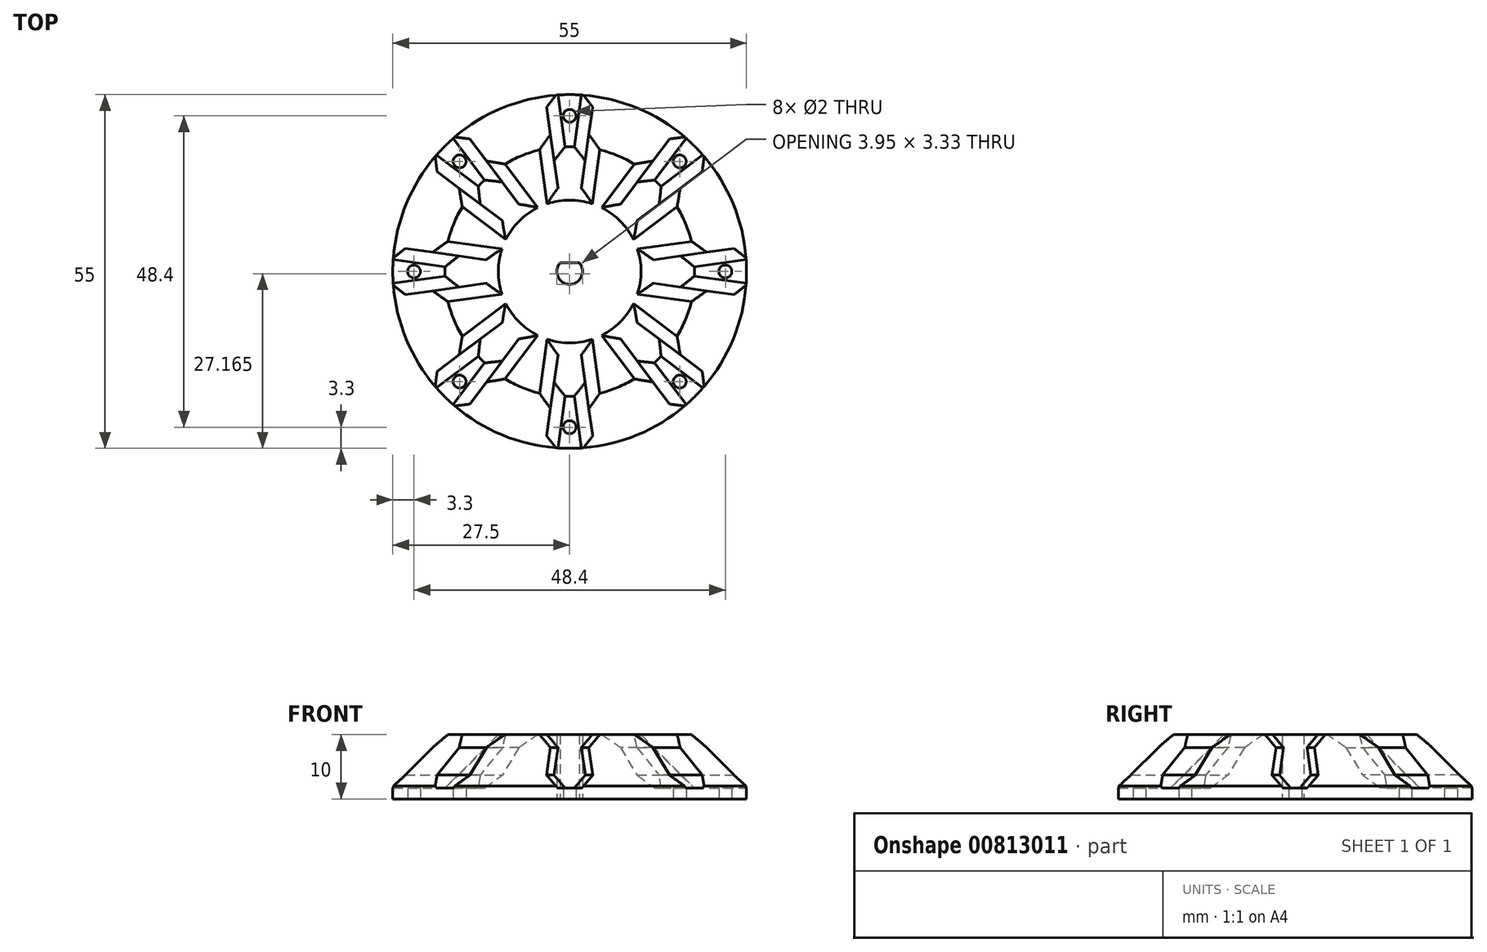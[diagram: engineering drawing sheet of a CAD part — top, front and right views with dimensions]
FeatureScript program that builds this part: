
annotation { "Feature Type Name" : "Feature", "Feature Type Description" : "" }
export const myFeature = defineFeature(function(context is Context, id is Id, definition is map)
    precondition{}
    {
        {
            var Q0;
            Q0=qCreatedBy(makeId("Top.planeOp"),FACE);
            var sketch = newSketch(context, id + "F0", { "sketchPlane" : qUnion([Q0])});
            skCircle(sketch, "E0", {"center": v(0, 0) * mm, "radius": 27.5 * mm});
            skCircle(sketch, "E1.0", {"center": v(0, 0) * mm, "radius": 21.1 * mm});
            skCircle(sketch, "E2", {"center": v(0, 24.2) * mm, "radius": 1 * mm});
            skCircle(sketch, "E3.1.0", {"center": v(-17.11, 17.11) * mm, "radius": 1 * mm});
            skCircle(sketch, "E3.2.0", {"center": v(-24.2, 0) * mm, "radius": 1 * mm});
            skCircle(sketch, "E3.3.0", {"center": v(-17.11, -17.11) * mm, "radius": 1 * mm});
            skCircle(sketch, "E3.4.0", {"center": v(0, -24.2) * mm, "radius": 1 * mm});
            skCircle(sketch, "E3.5.0", {"center": v(17.11, -17.11) * mm, "radius": 1 * mm});
            skCircle(sketch, "E3.6.0", {"center": v(24.2, 0) * mm, "radius": 1 * mm});
            skCircle(sketch, "E3.7.0", {"center": v(17.11, 17.11) * mm, "radius": 1 * mm});
            skLineSegment(sketch, "E4", {"start": v(0, 0) * mm, "end": v(3.83, 27.23) * mm});
            skLineSegment(sketch, "E5", {"start": v(0, 0) * mm, "end": v(16.55, 21.96) * mm});
            skLineSegment(sketch, "E6.1.0", {"start": v(0, 0) * mm, "end": v(-3.83, 27.23) * mm});
            skLineSegment(sketch, "E6.1.1", {"start": v(0, 0) * mm, "end": v(-16.55, 21.96) * mm});
            skLineSegment(sketch, "E6.2.0", {"start": v(0, 0) * mm, "end": v(-21.96, 16.55) * mm});
            skLineSegment(sketch, "E6.2.1", {"start": v(0, 0) * mm, "end": v(-27.23, 3.83) * mm});
            skLineSegment(sketch, "E6.3.0", {"start": v(0, 0) * mm, "end": v(-27.23, -3.83) * mm});
            skLineSegment(sketch, "E6.3.1", {"start": v(0, 0) * mm, "end": v(-21.96, -16.55) * mm});
            skLineSegment(sketch, "E6.4.0", {"start": v(0, 0) * mm, "end": v(-16.55, -21.96) * mm});
            skLineSegment(sketch, "E6.4.1", {"start": v(0, 0) * mm, "end": v(-3.83, -27.23) * mm});
            skLineSegment(sketch, "E6.5.0", {"start": v(0, 0) * mm, "end": v(3.83, -27.23) * mm});
            skLineSegment(sketch, "E6.5.1", {"start": v(0, 0) * mm, "end": v(16.55, -21.96) * mm});
            skLineSegment(sketch, "E6.6.0", {"start": v(0, 0) * mm, "end": v(21.96, -16.55) * mm});
            skLineSegment(sketch, "E6.6.1", {"start": v(0, 0) * mm, "end": v(27.23, -3.83) * mm});
            skLineSegment(sketch, "E6.7.0", {"start": v(0, 0) * mm, "end": v(27.23, 3.83) * mm});
            skLineSegment(sketch, "E6.7.1", {"start": v(0, 0) * mm, "end": v(21.96, 16.55) * mm});
            skSolve(sketch);
        }
        {
            var Q0;
            Q0=makeQuery(id+"F0.imprint","IMPRINT",FACE,{"disambiguationData":[TD([[makeQuery(id+"F0.imprint","IMPRINT",EDGE,{"derivedFrom":sQuery(id+"F0.wireOp",EDGE,"E0")}),1.0]])]});
            var Q1;
            Q1=makeQuery(id+"F0.imprint","IMPRINT",FACE,{"disambiguationData":[TD([[makeQuery(id+"F0.imprint","IMPRINT",EDGE,{"derivedFrom":sQuery(id+"F0.wireOp",EDGE,"E1.0")}),1.0]])]});
            var Q2;
            Q2=makeQuery(id+"F0.imprint","IMPRINT",FACE,{"disambiguationData":[TD([[makeQuery(id+"F0.imprint","IMPRINT",EDGE,{"derivedFrom":sQuery(id+"F0.wireOp",EDGE,"E3.1.0")}),-1.0]])]});
            var Q3;
            Q3=makeQuery(id+"F0.imprint","IMPRINT",FACE,{"disambiguationData":[TD([[makeQuery(id+"F0.imprint","IMPRINT",EDGE,{"derivedFrom":sQuery(id+"F0.wireOp",EDGE,"E2")}),-1.0]])]});
            var Q4;
            Q4=makeQuery(id+"F0.imprint","IMPRINT",FACE,{"disambiguationData":[TD([[makeQuery(id+"F0.imprint","IMPRINT",EDGE,{"derivedFrom":sQuery(id+"F0.wireOp",EDGE,"E3.7.0")}),-1.0]])]});
            var Q5;
            Q5=makeQuery(id+"F0.imprint","IMPRINT",FACE,{"disambiguationData":[TD([[makeQuery(id+"F0.imprint","IMPRINT",EDGE,{"derivedFrom":sQuery(id+"F0.wireOp",EDGE,"E3.6.0")}),-1.0]])]});
            var Q6;
            Q6=makeQuery(id+"F0.imprint","IMPRINT",FACE,{"disambiguationData":[TD([[makeQuery(id+"F0.imprint","IMPRINT",EDGE,{"derivedFrom":sQuery(id+"F0.wireOp",EDGE,"E3.5.0")}),-1.0]])]});
            var Q7;
            Q7=makeQuery(id+"F0.imprint","IMPRINT",FACE,{"disambiguationData":[TD([[makeQuery(id+"F0.imprint","IMPRINT",EDGE,{"derivedFrom":sQuery(id+"F0.wireOp",EDGE,"E3.4.0")}),-1.0]])]});
            var Q8;
            Q8=makeQuery(id+"F0.imprint","IMPRINT",FACE,{"disambiguationData":[TD([[makeQuery(id+"F0.imprint","IMPRINT",EDGE,{"derivedFrom":sQuery(id+"F0.wireOp",EDGE,"E3.3.0")}),-1.0]])]});
            var Q9;
            Q9=makeQuery(id+"F0.imprint","IMPRINT",FACE,{"disambiguationData":[TD([[makeQuery(id+"F0.imprint","IMPRINT",EDGE,{"derivedFrom":sQuery(id+"F0.wireOp",EDGE,"E3.2.0")}),-1.0]])]});
            extrude(context, id + "F1", {"entities" : qUnion([Q0, Q1, Q2, Q3, Q4, Q5, Q6, Q7, Q8, Q9]), "depth" : 1.7 * mm, "offsetDistance" : 25 * mm});
        }
        {
            var Q0;
            Q0=makeQuery(id+"F0.imprint","IMPRINT",FACE,{"disambiguationData":[TD([[makeQuery(id+"F0.imprint","IMPRINT",EDGE,{"derivedFrom":sQuery(id+"F0.wireOp",EDGE,"E1.0")}),1.0]])]});
            extrude(context, id + "F2", {"entities" : qUnion([Q0]), "operationType" : NewBodyOperationType.ADD, "depth" : 10 * mm, "offsetDistance" : 25 * mm});
        }
        {
            var Q0;
            Q0=makeQuery(id+"F2.opExtrude","CAP_EDGE",EDGE,{"disambiguationData":[OSD([sQuery(id+"F0.wireOp",EDGE,"E1.0")])],"isStart":false});
            chamfer(context, id + "F3", {"entities" : qUnion([Q0]), "width" : 10 * mm, "tangentPropagation" : true});
        }
        {
            var Q0;
            {var subQ0=sQuery(id+"F0.wireOp",EDGE,"E6.2.0");var subQ1=sQuery(id+"F0.wireOp",EDGE,"E0");var subQ2=makeQuery(id+"F0.imprint","INTERSECT",VERTEX,{"derivedFrom":[subQ1,subQ0]});Q0=makeQuery(id+"F0.imprint","IMPRINT",FACE,{"disambiguationData":[TD([[makeQuery(id+"F0.imprint","IMPRINT",EDGE,{"disambiguationData":[TD([[subQ2,-1.0]])],"derivedFrom":subQ1}),1.0]])]});}
            var Q1;
            {var subQ0=sQuery(id+"F0.wireOp",EDGE,"E6.2.0");var subQ1=sQuery(id+"F0.wireOp",EDGE,"E1.0");var subQ2=makeQuery(id+"F0.imprint","INTERSECT",VERTEX,{"derivedFrom":[subQ1,subQ0]});Q1=makeQuery(id+"F0.imprint","IMPRINT",FACE,{"disambiguationData":[TD([[makeQuery(id+"F0.imprint","IMPRINT",EDGE,{"disambiguationData":[TD([[subQ2,-1.0]])],"derivedFrom":subQ1}),1.0]])]});}
            var Q2;
            {var subQ0=sQuery(id+"F0.wireOp",EDGE,"E6.1.0");var subQ1=sQuery(id+"F0.wireOp",EDGE,"E0");var subQ2=makeQuery(id+"F0.imprint","INTERSECT",VERTEX,{"derivedFrom":[subQ1,subQ0]});Q2=makeQuery(id+"F0.imprint","IMPRINT",FACE,{"disambiguationData":[TD([[makeQuery(id+"F0.imprint","IMPRINT",EDGE,{"disambiguationData":[TD([[subQ2,-1.0]])],"derivedFrom":subQ1}),1.0]])]});}
            var Q3;
            {var subQ0=sQuery(id+"F0.wireOp",EDGE,"E6.1.0");var subQ1=sQuery(id+"F0.wireOp",EDGE,"E1.0");var subQ2=makeQuery(id+"F0.imprint","INTERSECT",VERTEX,{"derivedFrom":[subQ1,subQ0]});Q3=makeQuery(id+"F0.imprint","IMPRINT",FACE,{"disambiguationData":[TD([[makeQuery(id+"F0.imprint","IMPRINT",EDGE,{"disambiguationData":[TD([[subQ2,-1.0]])],"derivedFrom":subQ1}),1.0]])]});}
            var Q4;
            {var subQ0=sQuery(id+"F0.wireOp",EDGE,"E4");var subQ1=sQuery(id+"F0.wireOp",EDGE,"E0");var subQ2=makeQuery(id+"F0.imprint","INTERSECT",VERTEX,{"derivedFrom":[subQ1,subQ0]});Q4=makeQuery(id+"F0.imprint","IMPRINT",FACE,{"disambiguationData":[TD([[makeQuery(id+"F0.imprint","IMPRINT",EDGE,{"disambiguationData":[TD([[subQ2,1.0]])],"derivedFrom":subQ1}),1.0]])]});}
            var Q5;
            {var subQ0=sQuery(id+"F0.wireOp",EDGE,"E5");var subQ1=sQuery(id+"F0.wireOp",EDGE,"E1.0");var subQ2=makeQuery(id+"F0.imprint","INTERSECT",VERTEX,{"derivedFrom":[subQ1,subQ0]});Q5=makeQuery(id+"F0.imprint","IMPRINT",FACE,{"disambiguationData":[TD([[makeQuery(id+"F0.imprint","IMPRINT",EDGE,{"disambiguationData":[TD([[subQ2,-1.0]])],"derivedFrom":subQ1}),1.0]])]});}
            var Q6;
            {var subQ0=sQuery(id+"F0.wireOp",EDGE,"E6.7.0");var subQ1=sQuery(id+"F0.wireOp",EDGE,"E0");var subQ2=makeQuery(id+"F0.imprint","INTERSECT",VERTEX,{"derivedFrom":[subQ1,subQ0]});Q6=makeQuery(id+"F0.imprint","IMPRINT",FACE,{"disambiguationData":[TD([[makeQuery(id+"F0.imprint","IMPRINT",EDGE,{"disambiguationData":[TD([[subQ2,-1.0]])],"derivedFrom":subQ1}),1.0]])]});}
            var Q7;
            {var subQ0=sQuery(id+"F0.wireOp",EDGE,"E6.7.1");var subQ1=sQuery(id+"F0.wireOp",EDGE,"E1.0");var subQ2=makeQuery(id+"F0.imprint","INTERSECT",VERTEX,{"derivedFrom":[subQ1,subQ0]});Q7=makeQuery(id+"F0.imprint","IMPRINT",FACE,{"disambiguationData":[TD([[makeQuery(id+"F0.imprint","IMPRINT",EDGE,{"disambiguationData":[TD([[subQ2,1.0]])],"derivedFrom":subQ1}),1.0]])]});}
            var Q8;
            {var subQ0=sQuery(id+"F0.wireOp",EDGE,"E6.6.0");var subQ1=sQuery(id+"F0.wireOp",EDGE,"E0");var subQ2=makeQuery(id+"F0.imprint","INTERSECT",VERTEX,{"derivedFrom":[subQ1,subQ0]});Q8=makeQuery(id+"F0.imprint","IMPRINT",FACE,{"disambiguationData":[TD([[makeQuery(id+"F0.imprint","IMPRINT",EDGE,{"disambiguationData":[TD([[subQ2,-1.0]])],"derivedFrom":subQ1}),1.0]])]});}
            var Q9;
            {var subQ0=sQuery(id+"F0.wireOp",EDGE,"E6.6.0");var subQ1=sQuery(id+"F0.wireOp",EDGE,"E1.0");var subQ2=makeQuery(id+"F0.imprint","INTERSECT",VERTEX,{"derivedFrom":[subQ1,subQ0]});Q9=makeQuery(id+"F0.imprint","IMPRINT",FACE,{"disambiguationData":[TD([[makeQuery(id+"F0.imprint","IMPRINT",EDGE,{"disambiguationData":[TD([[subQ2,-1.0]])],"derivedFrom":subQ1}),1.0]])]});}
            var Q10;
            {var subQ0=sQuery(id+"F0.wireOp",EDGE,"E6.5.0");var subQ1=sQuery(id+"F0.wireOp",EDGE,"E0");var subQ2=makeQuery(id+"F0.imprint","INTERSECT",VERTEX,{"derivedFrom":[subQ1,subQ0]});Q10=makeQuery(id+"F0.imprint","IMPRINT",FACE,{"disambiguationData":[TD([[makeQuery(id+"F0.imprint","IMPRINT",EDGE,{"disambiguationData":[TD([[subQ2,-1.0]])],"derivedFrom":subQ1}),1.0]])]});}
            var Q11;
            {var subQ0=sQuery(id+"F0.wireOp",EDGE,"E6.5.0");var subQ1=sQuery(id+"F0.wireOp",EDGE,"E1.0");var subQ2=makeQuery(id+"F0.imprint","INTERSECT",VERTEX,{"derivedFrom":[subQ1,subQ0]});Q11=makeQuery(id+"F0.imprint","IMPRINT",FACE,{"disambiguationData":[TD([[makeQuery(id+"F0.imprint","IMPRINT",EDGE,{"disambiguationData":[TD([[subQ2,-1.0]])],"derivedFrom":subQ1}),1.0]])]});}
            var Q12;
            {var subQ0=sQuery(id+"F0.wireOp",EDGE,"E6.4.0");var subQ1=sQuery(id+"F0.wireOp",EDGE,"E1.0");var subQ2=makeQuery(id+"F0.imprint","INTERSECT",VERTEX,{"derivedFrom":[subQ1,subQ0]});Q12=makeQuery(id+"F0.imprint","IMPRINT",FACE,{"disambiguationData":[TD([[makeQuery(id+"F0.imprint","IMPRINT",EDGE,{"disambiguationData":[TD([[subQ2,-1.0]])],"derivedFrom":subQ1}),1.0]])]});}
            var Q13;
            {var subQ0=sQuery(id+"F0.wireOp",EDGE,"E6.4.0");var subQ1=sQuery(id+"F0.wireOp",EDGE,"E0");var subQ2=makeQuery(id+"F0.imprint","INTERSECT",VERTEX,{"derivedFrom":[subQ1,subQ0]});Q13=makeQuery(id+"F0.imprint","IMPRINT",FACE,{"disambiguationData":[TD([[makeQuery(id+"F0.imprint","IMPRINT",EDGE,{"disambiguationData":[TD([[subQ2,-1.0]])],"derivedFrom":subQ1}),1.0]])]});}
            var Q14;
            {var subQ0=sQuery(id+"F0.wireOp",EDGE,"E6.3.0");var subQ1=sQuery(id+"F0.wireOp",EDGE,"E0");var subQ2=makeQuery(id+"F0.imprint","INTERSECT",VERTEX,{"derivedFrom":[subQ1,subQ0]});Q14=makeQuery(id+"F0.imprint","IMPRINT",FACE,{"disambiguationData":[TD([[makeQuery(id+"F0.imprint","IMPRINT",EDGE,{"disambiguationData":[TD([[subQ2,-1.0]])],"derivedFrom":subQ1}),1.0]])]});}
            var Q15;
            {var subQ0=sQuery(id+"F0.wireOp",EDGE,"E6.3.0");var subQ1=sQuery(id+"F0.wireOp",EDGE,"E1.0");var subQ2=makeQuery(id+"F0.imprint","INTERSECT",VERTEX,{"derivedFrom":[subQ1,subQ0]});Q15=makeQuery(id+"F0.imprint","IMPRINT",FACE,{"disambiguationData":[TD([[makeQuery(id+"F0.imprint","IMPRINT",EDGE,{"disambiguationData":[TD([[subQ2,-1.0]])],"derivedFrom":subQ1}),1.0]])]});}
            extrude(context, id + "F4", {"entities" : qUnion([Q0, Q1, Q2, Q3, Q4, Q5, Q6, Q7, Q8, Q9, Q10, Q11, Q12, Q13, Q14, Q15]), "operationType" : NewBodyOperationType.ADD, "depth" : 10 * mm, "offsetDistance" : 25 * mm});
        }
        {
            var Q0;
            {var subQ0=sQuery(id+"F0.wireOp",EDGE,"E0");Q0=makeQuery(id+"F4.opExtrude","CAP_EDGE",EDGE,{"disambiguationData":[OSD([subQ0]),TDD([makeQuery(id+"F0.imprint","IMPRINT",EDGE,{"disambiguationData":[TD([[makeQuery(id+"F0.imprint","INTERSECT",VERTEX,{"derivedFrom":[subQ0,sQuery(id+"F0.wireOp",EDGE,"E6.2.0")]}),-1.0]])],"derivedFrom":subQ0})])],"isStart":false});}
            var Q1;
            {var subQ0=sQuery(id+"F0.wireOp",EDGE,"E0");Q1=makeQuery(id+"F4.opExtrude","CAP_EDGE",EDGE,{"disambiguationData":[OSD([subQ0]),TDD([makeQuery(id+"F0.imprint","IMPRINT",EDGE,{"disambiguationData":[TD([[makeQuery(id+"F0.imprint","INTERSECT",VERTEX,{"derivedFrom":[subQ0,sQuery(id+"F0.wireOp",EDGE,"E6.1.0")]}),-1.0]])],"derivedFrom":subQ0})])],"isStart":false});}
            var Q2;
            {var subQ0=sQuery(id+"F0.wireOp",EDGE,"E0");Q2=makeQuery(id+"F4.opExtrude","CAP_EDGE",EDGE,{"disambiguationData":[OSD([subQ0]),TDD([makeQuery(id+"F0.imprint","IMPRINT",EDGE,{"disambiguationData":[TD([[makeQuery(id+"F0.imprint","INTERSECT",VERTEX,{"derivedFrom":[subQ0,sQuery(id+"F0.wireOp",EDGE,"E4")]}),1.0]])],"derivedFrom":subQ0})])],"isStart":false});}
            var Q3;
            {var subQ0=sQuery(id+"F0.wireOp",EDGE,"E0");Q3=makeQuery(id+"F4.opExtrude","CAP_EDGE",EDGE,{"disambiguationData":[OSD([subQ0]),TDD([makeQuery(id+"F0.imprint","IMPRINT",EDGE,{"disambiguationData":[TD([[makeQuery(id+"F0.imprint","INTERSECT",VERTEX,{"derivedFrom":[subQ0,sQuery(id+"F0.wireOp",EDGE,"E6.7.0")]}),-1.0]])],"derivedFrom":subQ0})])],"isStart":false});}
            var Q4;
            {var subQ0=sQuery(id+"F0.wireOp",EDGE,"E0");Q4=makeQuery(id+"F4.opExtrude","CAP_EDGE",EDGE,{"disambiguationData":[OSD([subQ0]),TDD([makeQuery(id+"F0.imprint","IMPRINT",EDGE,{"disambiguationData":[TD([[makeQuery(id+"F0.imprint","INTERSECT",VERTEX,{"derivedFrom":[subQ0,sQuery(id+"F0.wireOp",EDGE,"E6.6.0")]}),-1.0]])],"derivedFrom":subQ0})])],"isStart":false});}
            var Q5;
            {var subQ0=sQuery(id+"F0.wireOp",EDGE,"E0");Q5=makeQuery(id+"F4.opExtrude","CAP_EDGE",EDGE,{"disambiguationData":[OSD([subQ0]),TDD([makeQuery(id+"F0.imprint","IMPRINT",EDGE,{"disambiguationData":[TD([[makeQuery(id+"F0.imprint","INTERSECT",VERTEX,{"derivedFrom":[subQ0,sQuery(id+"F0.wireOp",EDGE,"E6.5.0")]}),-1.0]])],"derivedFrom":subQ0})])],"isStart":false});}
            var Q6;
            {var subQ0=sQuery(id+"F0.wireOp",EDGE,"E0");Q6=makeQuery(id+"F4.opExtrude","CAP_EDGE",EDGE,{"disambiguationData":[OSD([subQ0]),TDD([makeQuery(id+"F0.imprint","IMPRINT",EDGE,{"disambiguationData":[TD([[makeQuery(id+"F0.imprint","INTERSECT",VERTEX,{"derivedFrom":[subQ0,sQuery(id+"F0.wireOp",EDGE,"E6.4.0")]}),-1.0]])],"derivedFrom":subQ0})])],"isStart":false});}
            var Q7;
            {var subQ0=sQuery(id+"F0.wireOp",EDGE,"E0");Q7=makeQuery(id+"F4.opExtrude","CAP_EDGE",EDGE,{"disambiguationData":[OSD([subQ0]),TDD([makeQuery(id+"F0.imprint","IMPRINT",EDGE,{"disambiguationData":[TD([[makeQuery(id+"F0.imprint","INTERSECT",VERTEX,{"derivedFrom":[subQ0,sQuery(id+"F0.wireOp",EDGE,"E6.3.0")]}),-1.0]])],"derivedFrom":subQ0})])],"isStart":false});}
            chamfer(context, id + "F5", {"entities" : qUnion([Q0, Q1, Q2, Q3, Q4, Q5, Q6, Q7]), "width" : 8 * mm, "tangentPropagation" : true});
        }
        {
            var Q0;
            Q0=makeQuery(id+"F4.boolean.opBoolean","INTERSECT",EDGE,{"derivedFrom":[makeQuery(id+"F1.opExtrude","CAP_FACE",FACE,{"disambiguationData":[OSD([sQuery(id+"F0.wireOp",EDGE,"E0"),sQuery(id+"F0.wireOp",EDGE,"E2"),sQuery(id+"F0.wireOp",EDGE,"E3.1.0"),sQuery(id+"F0.wireOp",EDGE,"E3.2.0"),sQuery(id+"F0.wireOp",EDGE,"E3.3.0"),sQuery(id+"F0.wireOp",EDGE,"E3.4.0"),sQuery(id+"F0.wireOp",EDGE,"E3.5.0"),sQuery(id+"F0.wireOp",EDGE,"E3.6.0"),sQuery(id+"F0.wireOp",EDGE,"E3.7.0")])],"isStart":false}),makeQuery(id+"F4.opExtrude","SWEPT_FACE",FACE,{"disambiguationData":[OSD([sQuery(id+"F0.wireOp",EDGE,"E6.7.1")])]})]});
            var Q1;
            Q1=makeQuery(id+"F4.boolean.opBoolean","INTERSECT",EDGE,{"derivedFrom":[makeQuery(id+"F1.opExtrude","CAP_FACE",FACE,{"disambiguationData":[OSD([sQuery(id+"F0.wireOp",EDGE,"E0"),sQuery(id+"F0.wireOp",EDGE,"E2"),sQuery(id+"F0.wireOp",EDGE,"E3.1.0"),sQuery(id+"F0.wireOp",EDGE,"E3.2.0"),sQuery(id+"F0.wireOp",EDGE,"E3.3.0"),sQuery(id+"F0.wireOp",EDGE,"E3.4.0"),sQuery(id+"F0.wireOp",EDGE,"E3.5.0"),sQuery(id+"F0.wireOp",EDGE,"E3.6.0"),sQuery(id+"F0.wireOp",EDGE,"E3.7.0")])],"isStart":false}),makeQuery(id+"F4.opExtrude","SWEPT_FACE",FACE,{"disambiguationData":[OSD([sQuery(id+"F0.wireOp",EDGE,"E5")])]})]});
            var Q2;
            Q2=makeQuery(id+"F4.boolean.opBoolean","INTERSECT",EDGE,{"derivedFrom":[makeQuery(id+"F1.opExtrude","CAP_FACE",FACE,{"disambiguationData":[OSD([sQuery(id+"F0.wireOp",EDGE,"E0"),sQuery(id+"F0.wireOp",EDGE,"E2"),sQuery(id+"F0.wireOp",EDGE,"E3.1.0"),sQuery(id+"F0.wireOp",EDGE,"E3.2.0"),sQuery(id+"F0.wireOp",EDGE,"E3.3.0"),sQuery(id+"F0.wireOp",EDGE,"E3.4.0"),sQuery(id+"F0.wireOp",EDGE,"E3.5.0"),sQuery(id+"F0.wireOp",EDGE,"E3.6.0"),sQuery(id+"F0.wireOp",EDGE,"E3.7.0")])],"isStart":false}),makeQuery(id+"F4.opExtrude","SWEPT_FACE",FACE,{"disambiguationData":[OSD([sQuery(id+"F0.wireOp",EDGE,"E6.7.0")])]})]});
            var Q3;
            Q3=makeQuery(id+"F4.boolean.opBoolean","INTERSECT",EDGE,{"derivedFrom":[makeQuery(id+"F1.opExtrude","CAP_FACE",FACE,{"disambiguationData":[OSD([sQuery(id+"F0.wireOp",EDGE,"E0"),sQuery(id+"F0.wireOp",EDGE,"E2"),sQuery(id+"F0.wireOp",EDGE,"E3.1.0"),sQuery(id+"F0.wireOp",EDGE,"E3.2.0"),sQuery(id+"F0.wireOp",EDGE,"E3.3.0"),sQuery(id+"F0.wireOp",EDGE,"E3.4.0"),sQuery(id+"F0.wireOp",EDGE,"E3.5.0"),sQuery(id+"F0.wireOp",EDGE,"E3.6.0"),sQuery(id+"F0.wireOp",EDGE,"E3.7.0")])],"isStart":false}),makeQuery(id+"F4.opExtrude","SWEPT_FACE",FACE,{"disambiguationData":[OSD([sQuery(id+"F0.wireOp",EDGE,"E6.6.1")])]})]});
            var Q4;
            Q4=makeQuery(id+"F4.boolean.opBoolean","INTERSECT",EDGE,{"derivedFrom":[makeQuery(id+"F1.opExtrude","CAP_FACE",FACE,{"disambiguationData":[OSD([sQuery(id+"F0.wireOp",EDGE,"E0"),sQuery(id+"F0.wireOp",EDGE,"E2"),sQuery(id+"F0.wireOp",EDGE,"E3.1.0"),sQuery(id+"F0.wireOp",EDGE,"E3.2.0"),sQuery(id+"F0.wireOp",EDGE,"E3.3.0"),sQuery(id+"F0.wireOp",EDGE,"E3.4.0"),sQuery(id+"F0.wireOp",EDGE,"E3.5.0"),sQuery(id+"F0.wireOp",EDGE,"E3.6.0"),sQuery(id+"F0.wireOp",EDGE,"E3.7.0")])],"isStart":false}),makeQuery(id+"F4.opExtrude","SWEPT_FACE",FACE,{"disambiguationData":[OSD([sQuery(id+"F0.wireOp",EDGE,"E6.6.0")])]})]});
            var Q5;
            Q5=makeQuery(id+"F4.boolean.opBoolean","INTERSECT",EDGE,{"derivedFrom":[makeQuery(id+"F1.opExtrude","CAP_FACE",FACE,{"disambiguationData":[OSD([sQuery(id+"F0.wireOp",EDGE,"E0"),sQuery(id+"F0.wireOp",EDGE,"E2"),sQuery(id+"F0.wireOp",EDGE,"E3.1.0"),sQuery(id+"F0.wireOp",EDGE,"E3.2.0"),sQuery(id+"F0.wireOp",EDGE,"E3.3.0"),sQuery(id+"F0.wireOp",EDGE,"E3.4.0"),sQuery(id+"F0.wireOp",EDGE,"E3.5.0"),sQuery(id+"F0.wireOp",EDGE,"E3.6.0"),sQuery(id+"F0.wireOp",EDGE,"E3.7.0")])],"isStart":false}),makeQuery(id+"F4.opExtrude","SWEPT_FACE",FACE,{"disambiguationData":[OSD([sQuery(id+"F0.wireOp",EDGE,"E6.5.1")])]})]});
            var Q6;
            Q6=makeQuery(id+"F4.boolean.opBoolean","INTERSECT",EDGE,{"derivedFrom":[makeQuery(id+"F1.opExtrude","CAP_FACE",FACE,{"disambiguationData":[OSD([sQuery(id+"F0.wireOp",EDGE,"E0"),sQuery(id+"F0.wireOp",EDGE,"E2"),sQuery(id+"F0.wireOp",EDGE,"E3.1.0"),sQuery(id+"F0.wireOp",EDGE,"E3.2.0"),sQuery(id+"F0.wireOp",EDGE,"E3.3.0"),sQuery(id+"F0.wireOp",EDGE,"E3.4.0"),sQuery(id+"F0.wireOp",EDGE,"E3.5.0"),sQuery(id+"F0.wireOp",EDGE,"E3.6.0"),sQuery(id+"F0.wireOp",EDGE,"E3.7.0")])],"isStart":false}),makeQuery(id+"F4.opExtrude","SWEPT_FACE",FACE,{"disambiguationData":[OSD([sQuery(id+"F0.wireOp",EDGE,"E6.5.0")])]})]});
            var Q7;
            Q7=makeQuery(id+"F4.boolean.opBoolean","INTERSECT",EDGE,{"derivedFrom":[makeQuery(id+"F1.opExtrude","CAP_FACE",FACE,{"disambiguationData":[OSD([sQuery(id+"F0.wireOp",EDGE,"E0"),sQuery(id+"F0.wireOp",EDGE,"E2"),sQuery(id+"F0.wireOp",EDGE,"E3.1.0"),sQuery(id+"F0.wireOp",EDGE,"E3.2.0"),sQuery(id+"F0.wireOp",EDGE,"E3.3.0"),sQuery(id+"F0.wireOp",EDGE,"E3.4.0"),sQuery(id+"F0.wireOp",EDGE,"E3.5.0"),sQuery(id+"F0.wireOp",EDGE,"E3.6.0"),sQuery(id+"F0.wireOp",EDGE,"E3.7.0")])],"isStart":false}),makeQuery(id+"F4.opExtrude","SWEPT_FACE",FACE,{"disambiguationData":[OSD([sQuery(id+"F0.wireOp",EDGE,"E6.4.1")])]})]});
            var Q8;
            Q8=makeQuery(id+"F4.boolean.opBoolean","INTERSECT",EDGE,{"derivedFrom":[makeQuery(id+"F1.opExtrude","CAP_FACE",FACE,{"disambiguationData":[OSD([sQuery(id+"F0.wireOp",EDGE,"E0"),sQuery(id+"F0.wireOp",EDGE,"E2"),sQuery(id+"F0.wireOp",EDGE,"E3.1.0"),sQuery(id+"F0.wireOp",EDGE,"E3.2.0"),sQuery(id+"F0.wireOp",EDGE,"E3.3.0"),sQuery(id+"F0.wireOp",EDGE,"E3.4.0"),sQuery(id+"F0.wireOp",EDGE,"E3.5.0"),sQuery(id+"F0.wireOp",EDGE,"E3.6.0"),sQuery(id+"F0.wireOp",EDGE,"E3.7.0")])],"isStart":false}),makeQuery(id+"F4.opExtrude","SWEPT_FACE",FACE,{"disambiguationData":[OSD([sQuery(id+"F0.wireOp",EDGE,"E6.4.0")])]})]});
            var Q9;
            Q9=makeQuery(id+"F4.boolean.opBoolean","INTERSECT",EDGE,{"derivedFrom":[makeQuery(id+"F1.opExtrude","CAP_FACE",FACE,{"disambiguationData":[OSD([sQuery(id+"F0.wireOp",EDGE,"E0"),sQuery(id+"F0.wireOp",EDGE,"E2"),sQuery(id+"F0.wireOp",EDGE,"E3.1.0"),sQuery(id+"F0.wireOp",EDGE,"E3.2.0"),sQuery(id+"F0.wireOp",EDGE,"E3.3.0"),sQuery(id+"F0.wireOp",EDGE,"E3.4.0"),sQuery(id+"F0.wireOp",EDGE,"E3.5.0"),sQuery(id+"F0.wireOp",EDGE,"E3.6.0"),sQuery(id+"F0.wireOp",EDGE,"E3.7.0")])],"isStart":false}),makeQuery(id+"F4.opExtrude","SWEPT_FACE",FACE,{"disambiguationData":[OSD([sQuery(id+"F0.wireOp",EDGE,"E6.3.1")])]})]});
            var Q10;
            Q10=makeQuery(id+"F4.boolean.opBoolean","INTERSECT",EDGE,{"derivedFrom":[makeQuery(id+"F1.opExtrude","CAP_FACE",FACE,{"disambiguationData":[OSD([sQuery(id+"F0.wireOp",EDGE,"E0"),sQuery(id+"F0.wireOp",EDGE,"E2"),sQuery(id+"F0.wireOp",EDGE,"E3.1.0"),sQuery(id+"F0.wireOp",EDGE,"E3.2.0"),sQuery(id+"F0.wireOp",EDGE,"E3.3.0"),sQuery(id+"F0.wireOp",EDGE,"E3.4.0"),sQuery(id+"F0.wireOp",EDGE,"E3.5.0"),sQuery(id+"F0.wireOp",EDGE,"E3.6.0"),sQuery(id+"F0.wireOp",EDGE,"E3.7.0")])],"isStart":false}),makeQuery(id+"F4.opExtrude","SWEPT_FACE",FACE,{"disambiguationData":[OSD([sQuery(id+"F0.wireOp",EDGE,"E6.3.0")])]})]});
            var Q11;
            Q11=makeQuery(id+"F4.boolean.opBoolean","INTERSECT",EDGE,{"derivedFrom":[makeQuery(id+"F1.opExtrude","CAP_FACE",FACE,{"disambiguationData":[OSD([sQuery(id+"F0.wireOp",EDGE,"E0"),sQuery(id+"F0.wireOp",EDGE,"E2"),sQuery(id+"F0.wireOp",EDGE,"E3.1.0"),sQuery(id+"F0.wireOp",EDGE,"E3.2.0"),sQuery(id+"F0.wireOp",EDGE,"E3.3.0"),sQuery(id+"F0.wireOp",EDGE,"E3.4.0"),sQuery(id+"F0.wireOp",EDGE,"E3.5.0"),sQuery(id+"F0.wireOp",EDGE,"E3.6.0"),sQuery(id+"F0.wireOp",EDGE,"E3.7.0")])],"isStart":false}),makeQuery(id+"F4.opExtrude","SWEPT_FACE",FACE,{"disambiguationData":[OSD([sQuery(id+"F0.wireOp",EDGE,"E6.2.1")])]})]});
            var Q12;
            Q12=makeQuery(id+"F4.boolean.opBoolean","INTERSECT",EDGE,{"derivedFrom":[makeQuery(id+"F1.opExtrude","CAP_FACE",FACE,{"disambiguationData":[OSD([sQuery(id+"F0.wireOp",EDGE,"E0"),sQuery(id+"F0.wireOp",EDGE,"E2"),sQuery(id+"F0.wireOp",EDGE,"E3.1.0"),sQuery(id+"F0.wireOp",EDGE,"E3.2.0"),sQuery(id+"F0.wireOp",EDGE,"E3.3.0"),sQuery(id+"F0.wireOp",EDGE,"E3.4.0"),sQuery(id+"F0.wireOp",EDGE,"E3.5.0"),sQuery(id+"F0.wireOp",EDGE,"E3.6.0"),sQuery(id+"F0.wireOp",EDGE,"E3.7.0")])],"isStart":false}),makeQuery(id+"F4.opExtrude","SWEPT_FACE",FACE,{"disambiguationData":[OSD([sQuery(id+"F0.wireOp",EDGE,"E6.2.0")])]})]});
            var Q13;
            Q13=makeQuery(id+"F4.boolean.opBoolean","INTERSECT",EDGE,{"derivedFrom":[makeQuery(id+"F1.opExtrude","CAP_FACE",FACE,{"disambiguationData":[OSD([sQuery(id+"F0.wireOp",EDGE,"E0"),sQuery(id+"F0.wireOp",EDGE,"E2"),sQuery(id+"F0.wireOp",EDGE,"E3.1.0"),sQuery(id+"F0.wireOp",EDGE,"E3.2.0"),sQuery(id+"F0.wireOp",EDGE,"E3.3.0"),sQuery(id+"F0.wireOp",EDGE,"E3.4.0"),sQuery(id+"F0.wireOp",EDGE,"E3.5.0"),sQuery(id+"F0.wireOp",EDGE,"E3.6.0"),sQuery(id+"F0.wireOp",EDGE,"E3.7.0")])],"isStart":false}),makeQuery(id+"F4.opExtrude","SWEPT_FACE",FACE,{"disambiguationData":[OSD([sQuery(id+"F0.wireOp",EDGE,"E6.1.1")])]})]});
            var Q14;
            Q14=makeQuery(id+"F4.boolean.opBoolean","INTERSECT",EDGE,{"derivedFrom":[makeQuery(id+"F1.opExtrude","CAP_FACE",FACE,{"disambiguationData":[OSD([sQuery(id+"F0.wireOp",EDGE,"E0"),sQuery(id+"F0.wireOp",EDGE,"E2"),sQuery(id+"F0.wireOp",EDGE,"E3.1.0"),sQuery(id+"F0.wireOp",EDGE,"E3.2.0"),sQuery(id+"F0.wireOp",EDGE,"E3.3.0"),sQuery(id+"F0.wireOp",EDGE,"E3.4.0"),sQuery(id+"F0.wireOp",EDGE,"E3.5.0"),sQuery(id+"F0.wireOp",EDGE,"E3.6.0"),sQuery(id+"F0.wireOp",EDGE,"E3.7.0")])],"isStart":false}),makeQuery(id+"F4.opExtrude","SWEPT_FACE",FACE,{"disambiguationData":[OSD([sQuery(id+"F0.wireOp",EDGE,"E6.1.0")])]})]});
            var Q15;
            Q15=makeQuery(id+"F4.boolean.opBoolean","INTERSECT",EDGE,{"derivedFrom":[makeQuery(id+"F1.opExtrude","CAP_FACE",FACE,{"disambiguationData":[OSD([sQuery(id+"F0.wireOp",EDGE,"E0"),sQuery(id+"F0.wireOp",EDGE,"E2"),sQuery(id+"F0.wireOp",EDGE,"E3.1.0"),sQuery(id+"F0.wireOp",EDGE,"E3.2.0"),sQuery(id+"F0.wireOp",EDGE,"E3.3.0"),sQuery(id+"F0.wireOp",EDGE,"E3.4.0"),sQuery(id+"F0.wireOp",EDGE,"E3.5.0"),sQuery(id+"F0.wireOp",EDGE,"E3.6.0"),sQuery(id+"F0.wireOp",EDGE,"E3.7.0")])],"isStart":false}),makeQuery(id+"F4.opExtrude","SWEPT_FACE",FACE,{"disambiguationData":[OSD([sQuery(id+"F0.wireOp",EDGE,"E4")])]})]});
            chamfer(context, id + "F6", {"entities" : qUnion([Q0, Q1, Q2, Q3, Q4, Q5, Q6, Q7, Q8, Q9, Q10, Q11, Q12, Q13, Q14, Q15]), "width" : 2 * mm, "tangentPropagation" : true});
        }
        {
            var Q0;
            Q0=makeQuery(id+"F4.opExtrude","CAP_EDGE",EDGE,{"disambiguationData":[OSD([sQuery(id+"F0.wireOp",EDGE,"E6.7.0")])],"isStart":false});
            var Q1;
            Q1=makeQuery(id+"F4.opExtrude","CAP_EDGE",EDGE,{"disambiguationData":[OSD([sQuery(id+"F0.wireOp",EDGE,"E6.7.1")])],"isStart":false});
            var Q2;
            Q2=makeQuery(id+"F4.opExtrude","CAP_EDGE",EDGE,{"disambiguationData":[OSD([sQuery(id+"F0.wireOp",EDGE,"E6.6.1")])],"isStart":false});
            var Q3;
            Q3=makeQuery(id+"F4.opExtrude","CAP_EDGE",EDGE,{"disambiguationData":[OSD([sQuery(id+"F0.wireOp",EDGE,"E6.6.0")])],"isStart":false});
            var Q4;
            Q4=makeQuery(id+"F4.opExtrude","CAP_EDGE",EDGE,{"disambiguationData":[OSD([sQuery(id+"F0.wireOp",EDGE,"E6.5.1")])],"isStart":false});
            var Q5;
            Q5=makeQuery(id+"F4.opExtrude","CAP_EDGE",EDGE,{"disambiguationData":[OSD([sQuery(id+"F0.wireOp",EDGE,"E6.5.0")])],"isStart":false});
            var Q6;
            Q6=makeQuery(id+"F4.opExtrude","CAP_EDGE",EDGE,{"disambiguationData":[OSD([sQuery(id+"F0.wireOp",EDGE,"E6.4.1")])],"isStart":false});
            var Q7;
            Q7=makeQuery(id+"F4.opExtrude","CAP_EDGE",EDGE,{"disambiguationData":[OSD([sQuery(id+"F0.wireOp",EDGE,"E6.4.0")])],"isStart":false});
            var Q8;
            Q8=makeQuery(id+"F4.opExtrude","CAP_EDGE",EDGE,{"disambiguationData":[OSD([sQuery(id+"F0.wireOp",EDGE,"E6.3.1")])],"isStart":false});
            var Q9;
            Q9=makeQuery(id+"F4.opExtrude","CAP_EDGE",EDGE,{"disambiguationData":[OSD([sQuery(id+"F0.wireOp",EDGE,"E6.3.0")])],"isStart":false});
            var Q10;
            Q10=makeQuery(id+"F4.opExtrude","CAP_EDGE",EDGE,{"disambiguationData":[OSD([sQuery(id+"F0.wireOp",EDGE,"E6.2.1")])],"isStart":false});
            var Q11;
            Q11=makeQuery(id+"F4.opExtrude","CAP_EDGE",EDGE,{"disambiguationData":[OSD([sQuery(id+"F0.wireOp",EDGE,"E6.2.0")])],"isStart":false});
            var Q12;
            Q12=makeQuery(id+"F4.opExtrude","CAP_EDGE",EDGE,{"disambiguationData":[OSD([sQuery(id+"F0.wireOp",EDGE,"E6.1.1")])],"isStart":false});
            var Q13;
            Q13=makeQuery(id+"F4.opExtrude","CAP_EDGE",EDGE,{"disambiguationData":[OSD([sQuery(id+"F0.wireOp",EDGE,"E6.1.0")])],"isStart":false});
            var Q14;
            Q14=makeQuery(id+"F4.opExtrude","CAP_EDGE",EDGE,{"disambiguationData":[OSD([sQuery(id+"F0.wireOp",EDGE,"E4")])],"isStart":false});
            var Q15;
            Q15=makeQuery(id+"F4.opExtrude","CAP_EDGE",EDGE,{"disambiguationData":[OSD([sQuery(id+"F0.wireOp",EDGE,"E5")])],"isStart":false});
            chamfer(context, id + "F7", {"entities" : qUnion([Q0, Q1, Q2, Q3, Q4, Q5, Q6, Q7, Q8, Q9, Q10, Q11, Q12, Q13, Q14, Q15]), "width" : 2 * mm, "tangentPropagation" : true});
        }
        {
            var Q0;
            Q0=qCreatedBy(makeId("Top.planeOp"),FACE);
            var sketch = newSketch(context, id + "F8", { "sketchPlane" : qUnion([Q0])});
            skArc(sketch, "E7", {"start": v(-1.5, 1.33) * mm, "mid": v(0, -2) * mm, "end": v(1.5, 1.33) * mm});
            skLineSegment(sketch, "E8", {"start": v(-1.5, 1.33) * mm, "end": v(1.5, 1.33) * mm});
            skSolve(sketch);
        }
        {
            var Q0;
            Q0=makeQuery(id+"F8.imprint","IMPRINT",FACE,{"disambiguationData":[TD([[makeQuery(id+"F8.imprint","IMPRINT",EDGE,{"derivedFrom":sQuery(id+"F8.wireOp",EDGE,"E7")}),1.0]])]});
            extrude(context, id + "F9", {"entities" : qUnion([Q0]), "operationType" : NewBodyOperationType.REMOVE, "depth" : 10 * mm, "offsetDistance" : 25 * mm});
        }
    });
